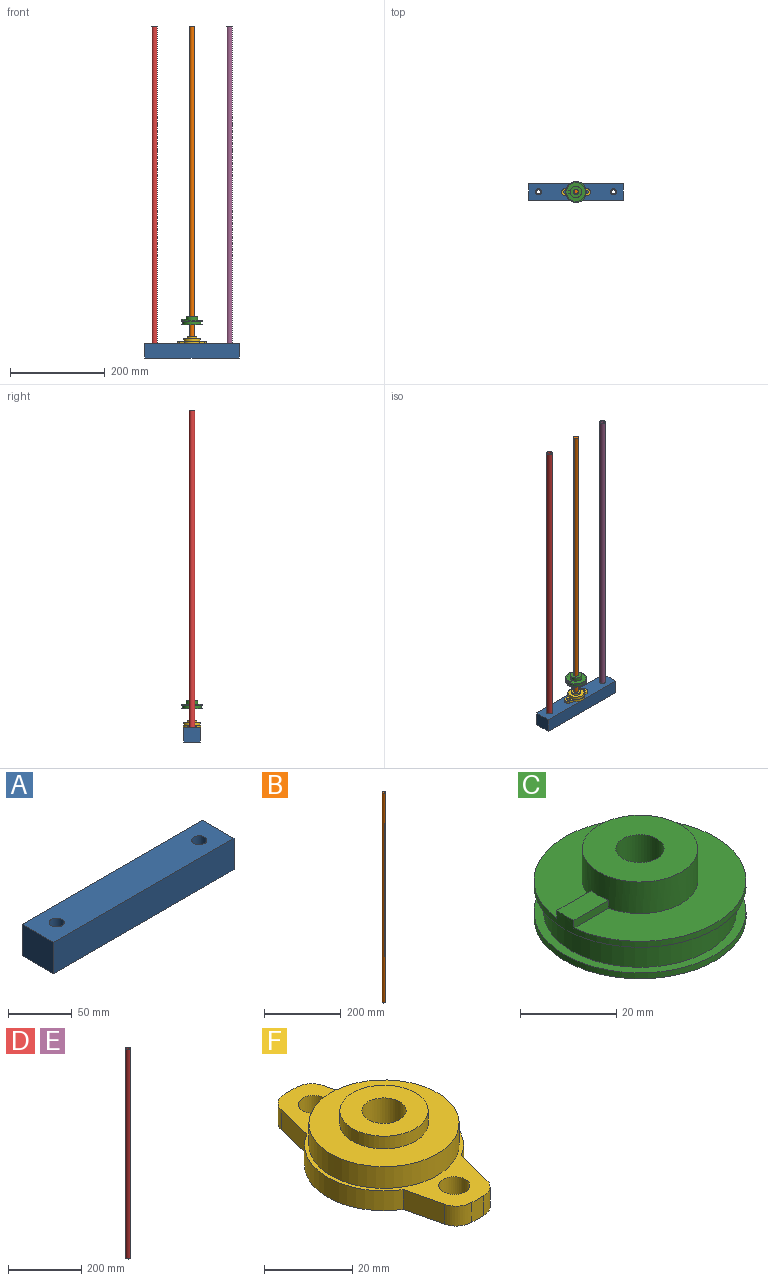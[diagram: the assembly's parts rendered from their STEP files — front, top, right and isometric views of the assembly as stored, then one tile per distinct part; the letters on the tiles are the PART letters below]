
ASSEMBLY  parts=6 mates=5
PART A: 8 faces, bbox 200x35x30 mm
  f0: plane 35x30mm, normal (1,0,0), area 1050mm2, adj f1,f4,f6,f7
  f1: plane 200x30mm, normal (0,1,0), area 6000mm2, adj f0,f2,f6,f7
  f2: plane 35x30mm, normal (-1,0,0), area 1050mm2, adj f1,f4,f6,f7
  f3: cylinder r=6mm len=30mm, axis (0,0,-1), area 1131mm2, adj f6,f7
  f4: plane 200x30mm, normal (0,-1,0), area 6000mm2, adj f0,f2,f6,f7
  f5: cylinder r=6mm len=30mm, axis (0,0,-1), area 1131mm2, adj f6,f7
  f6: plane 200x35mm, normal (0,0,1), area 6773.8mm2, adj f0,f1,f2,f3,f4,f5
  f7: plane 200x35mm, normal (0,0,-1), area 6773.8mm2, adj f0,f1,f2,f3,f4,f5
PART B: 6 faces, bbox 10x9.9x670 mm
  f0: cylinder r=5mm len=670mm, axis (0,0,-1), area 19699.6mm2, adj f1,f2,f3,f4
  f1: plane 10x9.9mm, normal (0,0,1), area 76.6mm2, adj f0,f3,f4,f5
  f2: plane 10x9.9mm, normal (0,0,-1), area 76.6mm2, adj f0,f3,f4,f5
  f3: plane 670x0.9mm, normal (-1,0,0), area 602.3mm2, adj f0,f1,f2,f5
  f4: plane 670x0.9mm, normal (1,0,0), area 602.3mm2, adj f0,f1,f2,f5
  f5: plane 670x2mm, normal (0,-1,0), area 1340mm2, adj f1,f2,f3,f4
PART C: 13 faces, bbox 44x44x17.5 mm
  f0: cylinder r=12mm len=24mm, axis (0,0,-1), area 593.1mm2, adj f7,f8,f10,f11,f12
  f1: plane 44x44mm, normal (0,0,-1), area 1442mm2, adj f2,f9
  f2: cylinder r=22mm len=44mm, axis (0,0,-1), area 207.3mm2, adj f1,f3
  f3: plane 44x44mm, normal (0,0,1), area 263.9mm2, adj f2,f4
  f4: cylinder r=20mm len=40mm, axis (0,0,-1), area 816.8mm2, adj f3,f5
  f5: plane 44x44mm, normal (0,0,-1), area 263.9mm2, adj f4,f6
  f6: cylinder r=22mm len=44mm, axis (0,0,-1), area 217.4mm2, adj f5,f7,f10,f11,f12
  f7: plane 44x43.86mm, normal (0,0,1), area 1017.9mm2, adj f0,f6,f10,f11
  f8: plane 24x24mm, normal (0,0,1), area 373.8mm2, adj f0,f9
  f9: cylinder r=5mm len=17.5mm, axis (0,0,1), area 549.8mm2, adj f1,f8
  f10: plane 10.12x2mm, normal (0,1,0), area 20.2mm2, adj f0,f6,f7,f12
  f11: plane 10.12x2mm, normal (0,-1,0), area 20.2mm2, adj f0,f6,f7,f12
  f12: plane 10.26x5mm, normal (0,0,1), area 50.2mm2, adj f0,f6,f10,f11
PART D: 4 faces, bbox 12x12x700 mm
  f0: cylinder r=5mm len=700mm, axis (0,0,-1), area 21991.1mm2, adj f2,f3
  f1: cylinder r=6mm len=700mm, axis (0,0,-1), area 26389.4mm2, adj f2,f3
  f2: plane 12x12mm, normal (0,0,1), area 34.6mm2, adj f0,f1
  f3: plane 12x12mm, normal (0,0,-1), area 34.6mm2, adj f0,f1
PART E: same geometry as D
PART F: 21 faces, bbox 36x60x15 mm
  f0: plane 10.76x5.5mm, normal (-0.97,0.23,0), area 60.9mm2, adj f1,f10,f11,f20
  f1: cylinder r=18mm len=30.81mm, axis (0,0,-1), area 203.4mm2, adj f0,f2,f10,f11
  f2: plane 10.76x5.5mm, normal (-0.97,-0.23,0), area 60.9mm2, adj f1,f10,f11,f17
  f3: plane 5.5x3.72mm, normal (0,-1,0), area 20.5mm2, adj f10,f11,f17,f18
  f4: plane 10.76x5.5mm, normal (0.97,-0.23,0), area 60.9mm2, adj f5,f10,f11,f18
  f5: cylinder r=18mm len=30.81mm, axis (0,0,-1), area 203.4mm2, adj f4,f6,f10,f11
  f6: plane 10.76x5.5mm, normal (0.97,0.23,0), area 60.9mm2, adj f5,f10,f11,f19
  f7: cylinder r=3.5mm len=7mm, axis (0,0,-1), area 121mm2, adj f10,f11
  f8: plane 5.5x3.72mm, normal (0,1,0), area 20.5mm2, adj f10,f11,f19,f20
  f9: cylinder r=3.5mm len=7mm, axis (0,0,-1), area 121mm2, adj f10,f11
  f10: plane 60x36mm, normal (0,0,1), area 396.5mm2, adj f0,f1,f2,f3,f4,f5,f6,f7
  f11: plane 60x36mm, normal (0,0,-1), area 1225.9mm2, adj f0,f1,f2,f3,f4,f5,f6,f7
  f12: cylinder r=17mm len=34mm, axis (0,0,-1), area 640.9mm2, adj f10,f13
  f13: plane 34x34mm, normal (0,0,1), area 593.8mm2, adj f12,f15
  f14: cylinder r=5mm len=15mm, axis (0,0,-1), area 471.2mm2, adj f11,f16
  f15: cylinder r=10mm len=20mm, axis (0,0,-1), area 219.9mm2, adj f13,f16
  f16: plane 20x20mm, normal (0,0,1), area 235.6mm2, adj f14,f15
  f17: cylinder r=5mm len=5.5mm, axis (0,0,-1), area 36.7mm2, adj f2,f3,f10,f11
  f18: cylinder r=5mm len=5.5mm, axis (0,0,-1), area 36.7mm2, adj f3,f4,f10,f11
  f19: cylinder r=5mm len=5.5mm, axis (0,0,-1), area 36.7mm2, adj f6,f8,f10,f11
  f20: cylinder r=5mm len=5.5mm, axis (0,0,-1), area 36.7mm2, adj f0,f8,f10,f11
PLACE A t=(55.93,-0.19,-97.45)mm
PLACE B rot(axis=(0,0,-1),90deg) t=(55.93,-0.19,-67.45)mm
PLACE C t=(55.93,-0.19,-27.45)mm
PLACE D t=(-23.07,-0.19,-97.45)mm
PLACE E t=(134.93,-0.19,-97.45)mm
PLACE F rot(axis=(0,0,1),90deg) t=(55.93,-0.19,-67.45)mm
MATE fastened E.f0 <-> A.f5  axis (0,0,-1) through (134.93,-0.19,-97.45)mm
MATE fastened B.f0 <-> C.f9  axis (0,0,-1) through (55.93,-0.19,-67.45)mm
MATE revolute B.f0 <-> F.f14  axis (0,0,-1) through (55.93,-0.19,-67.45)mm
MATE fastened A.f3 <-> D.f1  axis (0,0,-1) through (-23.07,-0.19,-97.45)mm
MATE fastened F.f14 <-> A.f6  axis (0,0,-1) through (55.93,-0.19,-67.45)mm
